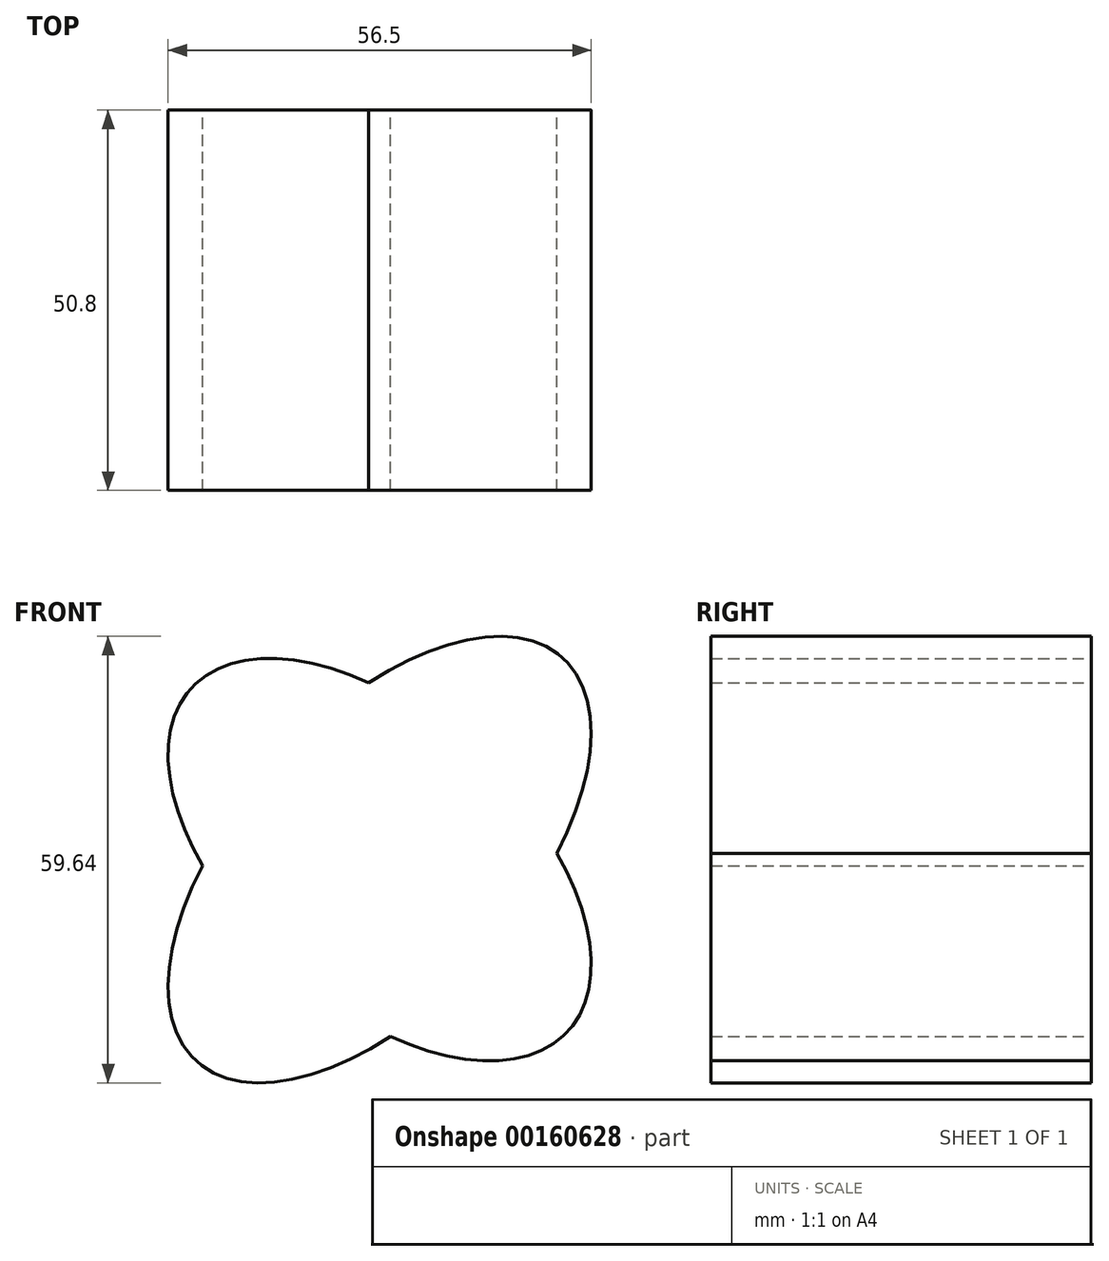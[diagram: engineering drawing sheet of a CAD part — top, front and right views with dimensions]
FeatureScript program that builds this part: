
annotation { "Feature Type Name" : "Feature", "Feature Type Description" : "" }
export const myFeature = defineFeature(function(context is Context, id is Id, definition is map)
    precondition{}
    {
        {
            var Q0;
            Q0=qCreatedBy(makeId("Front.planeOp"),FACE);
            var sketch = newSketch(context, id + "F0", { "sketchPlane" : qUnion([Q0])});
            skEllipticalArc(sketch, "E0", {});
            skEllipticalArc(sketch, "E1", {});
            skLineSegment(sketch, "E2", {"start": v(-24.47, -26.93) * mm, "end": v(24.47, 26.93) * mm, "construction": true});
            skLineSegment(sketch, "E3", {"start": v(25.18, -22.88) * mm, "end": v(-25.18, 22.88) * mm, "construction": true});
            skEllipticalArc(sketch, "E4.trimOffspring", {});
            skEllipticalArc(sketch, "E5.trimOffspring", {});
            const initialGuessF0  = {"E0": [0, 0, 0.6725052816597334, 0.7400923227137023, 0.0363840118775876, 0.01905, 2.041775232270425, 4.241410074909162], "E1": [0, 0, -0.7400923227137021, 0.6725052816597336, 0.03402485038023082, 0.01905, 5.234749399378142, 1.0484359078014442], "E4.trimOffspring": [0, 0, -0.7400923227137021, 0.6725052816597336, 0.03402485038023082, 0.01905, 2.093156745788349, 4.190028561391237], "E5.trimOffspring": [0, 0, 0.6725052816597334, 0.7400923227137023, 0.0363840118775876, 0.01905, 5.183367885860218, 1.0998174213193683]};
            skSetInitialGuess(sketch, initialGuessF0);
            skSolve(sketch);
        }
        {
            var Q0;
            Q0=qSketchRegion(id+"F0",true);
            extrude(context, id + "F1", {"entities" : qUnion([Q0]), "depth" : 25.4 * mm});
        }
        {
            var Q0;
            Q0=makeQuery(id+"F1.opExtrude","CAP_FACE",FACE,{"disambiguationData":[OSD([sQuery(id+"F0.wireOp",EDGE,"E0"),sQuery(id+"F0.wireOp",EDGE,"E1"),sQuery(id+"F0.wireOp",EDGE,"E4.trimOffspring"),sQuery(id+"F0.wireOp",EDGE,"E5.trimOffspring")])],"isStart":false});
            extrude(context, id + "F2", {"entities" : qUnion([Q0]), "operationType" : NewBodyOperationType.ADD, "depth" : 25.4 * mm});
        }
    });
